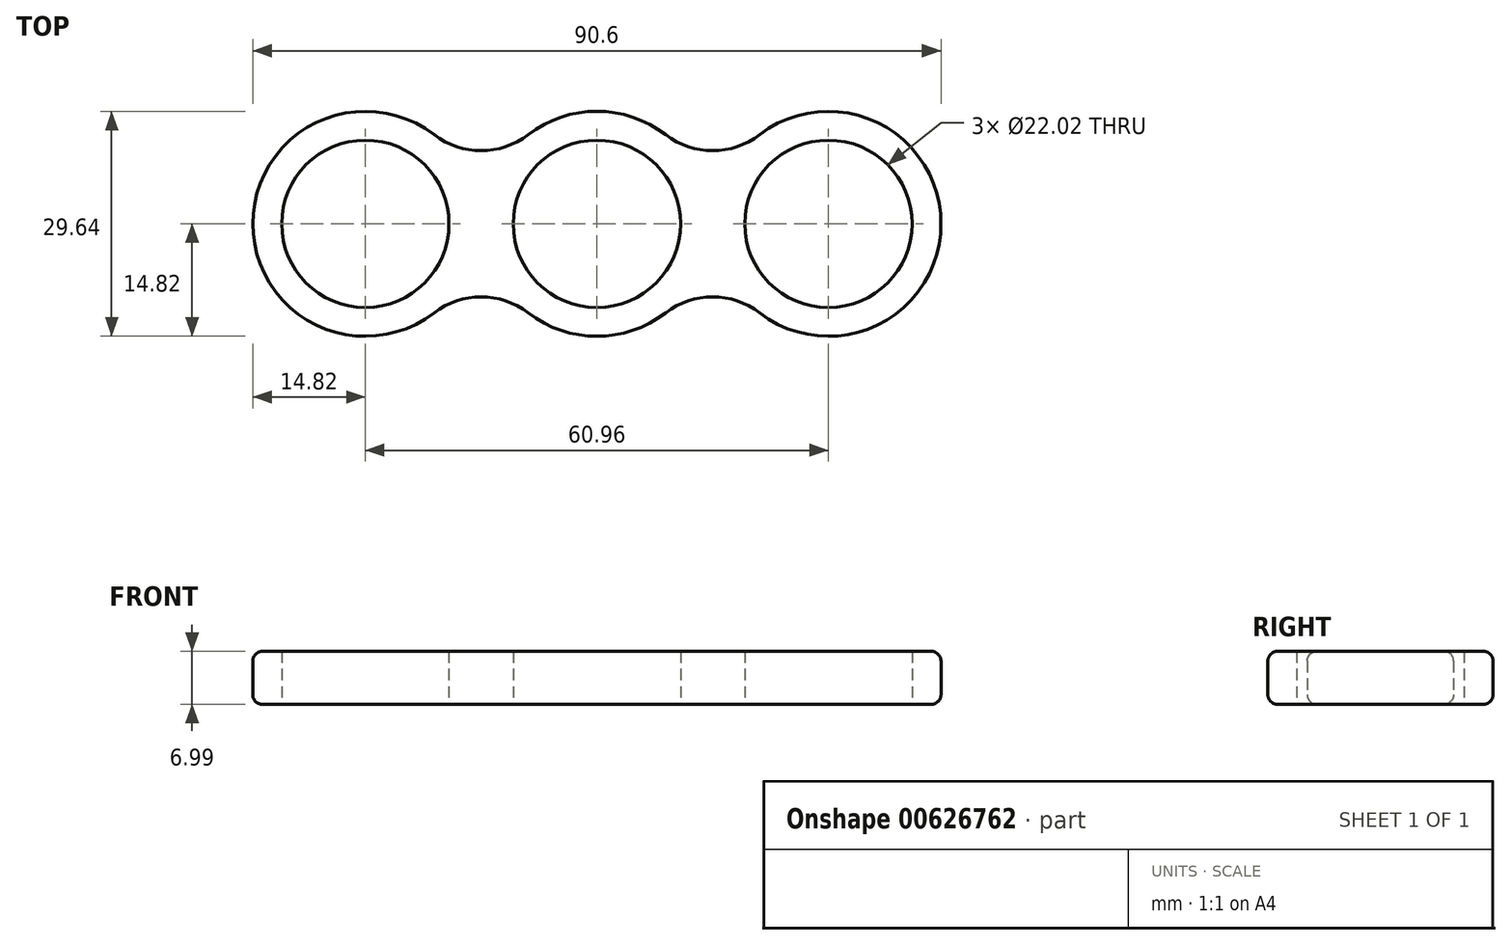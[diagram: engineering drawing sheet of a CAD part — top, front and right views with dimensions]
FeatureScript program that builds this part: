
annotation { "Feature Type Name" : "Feature", "Feature Type Description" : "" }
export const myFeature = defineFeature(function(context is Context, id is Id, definition is map)
    precondition{}
    {
        {
            var Q0;
            Q0=qCreatedBy(makeId("Top.planeOp"),FACE);
            var sketch = newSketch(context, id + "F0", { "sketchPlane" : qUnion([Q0])});
            skCircle(sketch, "E0", {"center": v(0, 0) * mm, "radius": 11.01 * mm});
            skCircle(sketch, "E1", {"center": v(-30.48, 0) * mm, "radius": 11.01 * mm});
            skCircle(sketch, "E2", {"center": v(30.48, 0) * mm, "radius": 11.01 * mm});
            skLineSegment(sketch, "E3", {"start": v(30.48, 0) * mm, "end": v(0, 0) * mm});
            skLineSegment(sketch, "E4", {"start": v(0, 0) * mm, "end": v(-30.48, 0) * mm});
            skCircle(sketch, "E5", {"center": v(30.48, 0) * mm, "radius": 14.82 * mm});
            skCircle(sketch, "E6", {"center": v(0, 0) * mm, "radius": 14.82 * mm});
            skCircle(sketch, "E7", {"center": v(-30.48, 0) * mm, "radius": 14.82 * mm});
            skArc(sketch, "E8", {"start": v(21.44, -11.74) * mm, "mid": v(15.24, -9.63) * mm, "end": v(9.04, -11.74) * mm});
            skArc(sketch, "E9", {"start": v(-9.04, -11.74) * mm, "mid": v(-15.24, -9.63) * mm, "end": v(-21.44, -11.74) * mm});
            skArc(sketch, "E10", {"start": v(9.04, 11.74) * mm, "mid": v(15.24, 9.63) * mm, "end": v(21.44, 11.74) * mm});
            skArc(sketch, "E11", {"start": v(-21.44, 11.74) * mm, "mid": v(-15.24, 9.63) * mm, "end": v(-9.04, 11.74) * mm});
            skSolve(sketch);
        }
        {
            var Q0;
            Q0 = qSketchRegion(id + "F0", true);
            extrude(context, id + "F1", {"entities" : qUnion([Q0]), "depth" : 7 * mm, "offsetDistance" : 25.4 * mm});
        }
        {
            var Q0;
            Q0=makeQuery(id+"F1.opExtrude","SWEPT_EDGE",EDGE,{"disambiguationData":[OSD([sQuery(id+"F0.wireOp",EDGE,"E7"),sQuery(id+"F0.wireOp",EDGE,"E9")])]});
            var Q1;
            Q1=makeQuery(id+"F1.opExtrude","CAP_EDGE",EDGE,{"disambiguationData":[OSD([sQuery(id+"F0.wireOp",EDGE,"E11")])],"isStart":false});
            fillet(context, id + "F2", {"entities" : qUnion([Q0, Q1]), "radius" : 1.27 * mm, "tangentPropagation" : true, "allowEdgeOverflow" : false});
        }
        {
            var Q0;
            {var subQ0=sQuery(id+"F0.wireOp",EDGE,"E6");Q0=makeQuery(id+"F1.opExtrude","CAP_EDGE",EDGE,{"disambiguationData":[OSD([subQ0]),TDD([makeQuery(id+"F0.imprint","IMPRINT",EDGE,{"disambiguationData":[TD([[makeQuery(id+"F0.imprint","INTERSECT",VERTEX,{"derivedFrom":[subQ0,sQuery(id+"F0.wireOp",EDGE,"E8")]}),1.0]])],"derivedFrom":subQ0})])],"isStart":true});}
            fillet(context, id + "F3", {"entities" : qUnion([Q0]), "radius" : 1.27 * mm, "tangentPropagation" : true, "allowEdgeOverflow" : false});
        }
    });
